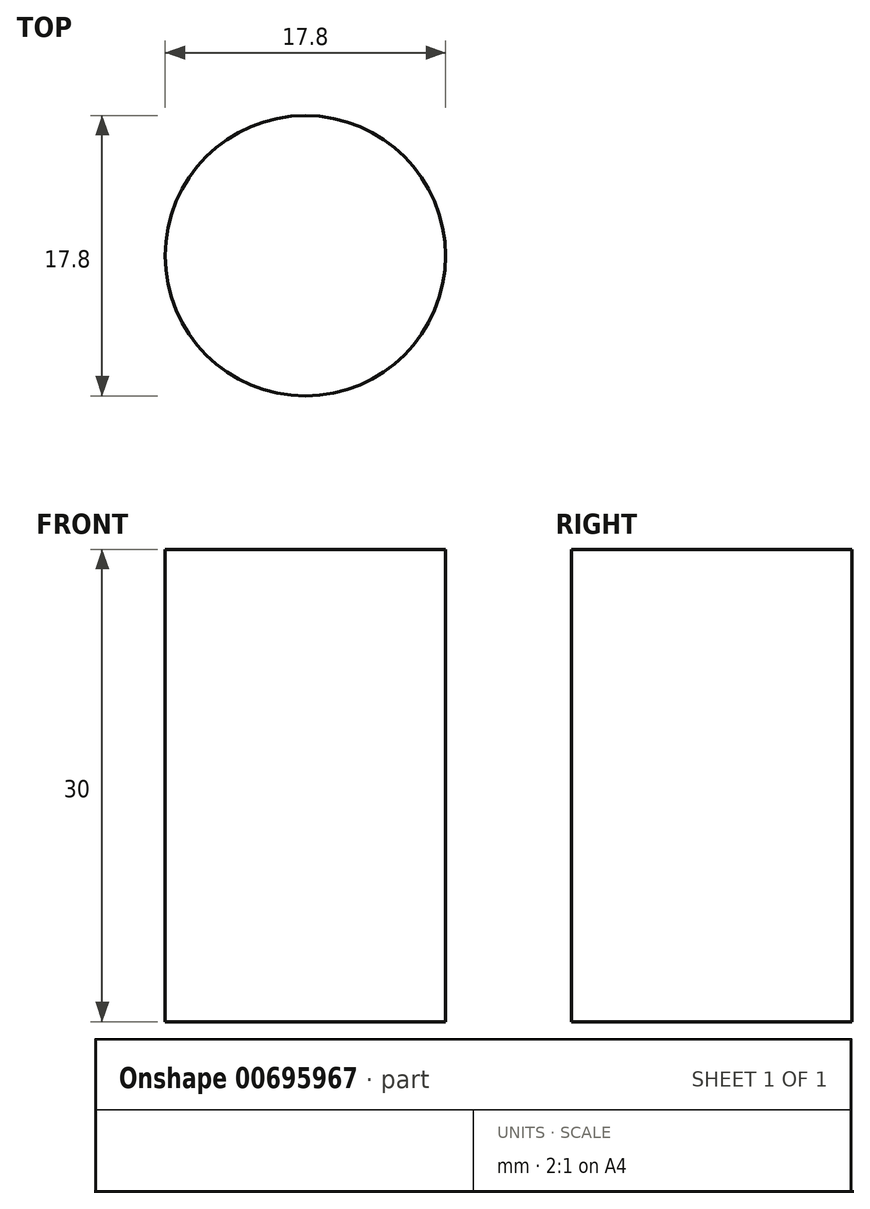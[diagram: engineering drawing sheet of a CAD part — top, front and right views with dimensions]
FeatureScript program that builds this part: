
annotation { "Feature Type Name" : "Feature", "Feature Type Description" : "" }
export const myFeature = defineFeature(function(context is Context, id is Id, definition is map)
    precondition{}
    {
        {
            var Q0;
            Q0=qCreatedBy(makeId("Top.planeOp"),FACE);
            var sketch = newSketch(context, id + "F0", { "sketchPlane" : qUnion([Q0])});
            skCircle(sketch, "E0", {"center": v(0, 0) * mm, "radius": 8.9 * mm});
            skSolve(sketch);
        }
        {
            var Q0;
            Q0 = qSketchRegion(id + "F0", true);
            extrude(context, id + "F1", {"entities" : qUnion([Q0]), "depth" : 30 * mm, "offsetDistance" : 25 * mm});
        }
    });
